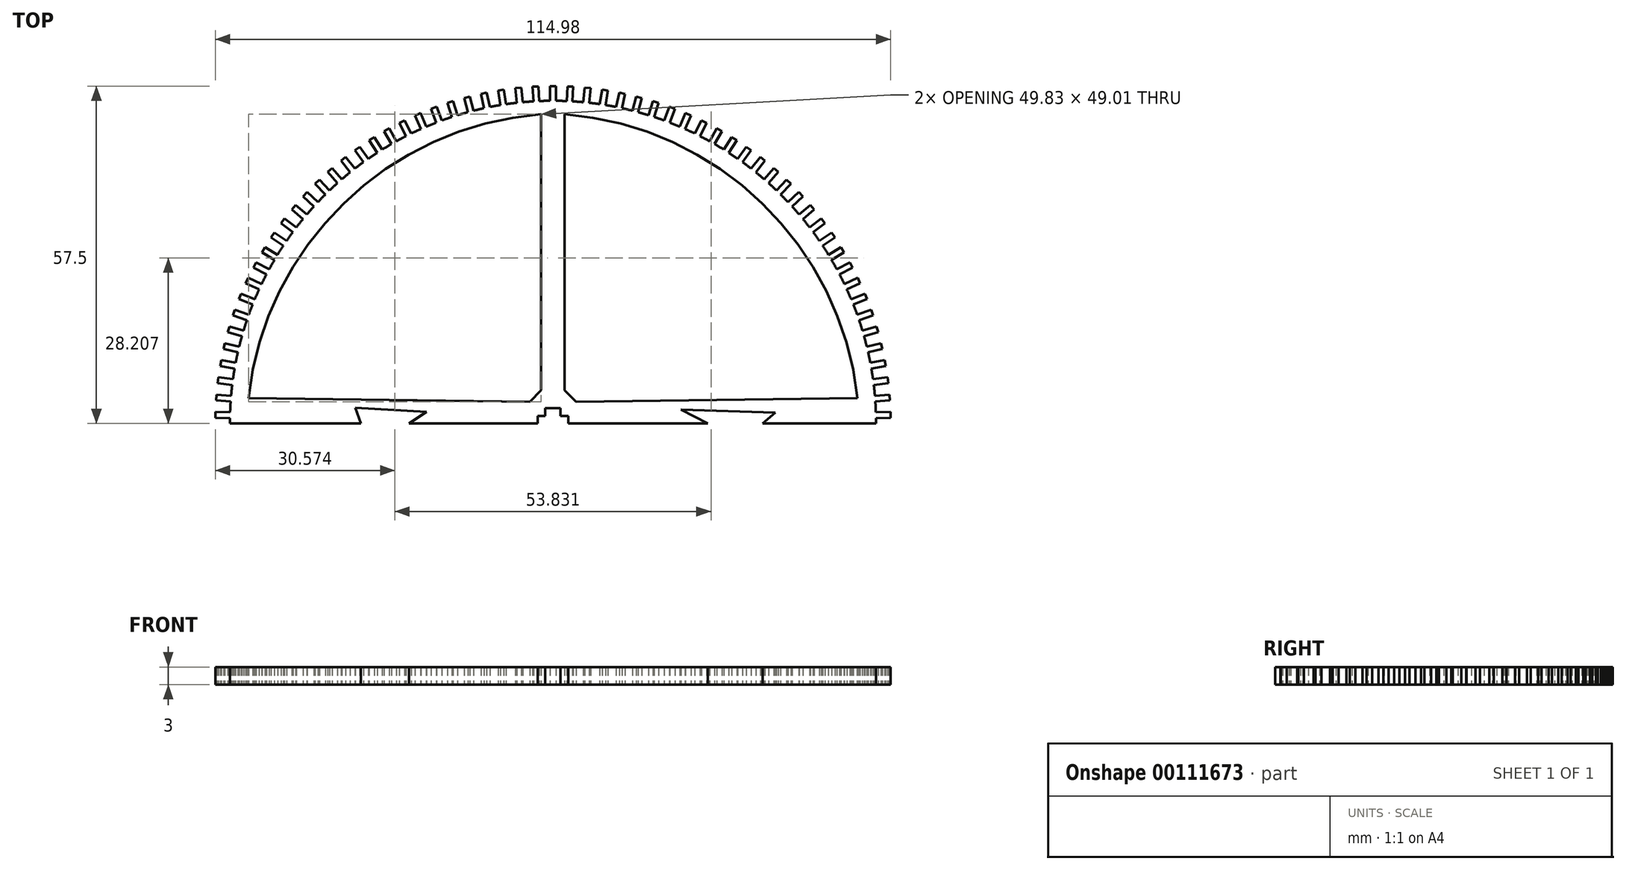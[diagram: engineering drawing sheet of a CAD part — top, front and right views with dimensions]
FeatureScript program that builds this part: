
annotation { "Feature Type Name" : "Feature", "Feature Type Description" : "" }
export const myFeature = defineFeature(function(context is Context, id is Id, definition is map)
    precondition{}
    {
        {
            var Q0;
            Q0=qCreatedBy(makeId("Top.planeOp"),FACE);
            var sketch = newSketch(context, id + "F0", { "sketchPlane" : qUnion([Q0])});
            skArc(sketch, "E0", {"start": v(55, 0.92) * mm, "mid": v(0, 55) * mm, "end": v(-55, 0.92) * mm});
            skLineSegment(sketch, "E1", {"start": v(0, 2.6) * mm, "end": v(1.3, 2.6) * mm});
            skLineSegment(sketch, "E2", {"start": v(1.3, 2.6) * mm, "end": v(1.3, 1.3) * mm});
            skLineSegment(sketch, "E3", {"start": v(1.3, 1.3) * mm, "end": v(2.6, 1.3) * mm});
            skLineSegment(sketch, "E4", {"start": v(2.6, 1.3) * mm, "end": v(2.6, 0) * mm});
            skLineSegment(sketch, "E5", {"start": v(-2.6, 1.3) * mm, "end": v(-1.3, 1.3) * mm});
            skLineSegment(sketch, "E6", {"start": v(-1.3, 1.3) * mm, "end": v(-1.3, 2.6) * mm});
            skLineSegment(sketch, "E7", {"start": v(-1.3, 2.6) * mm, "end": v(0, 2.6) * mm});
            skPoint(sketch, "E8.start.orphan", {"position": v(-51.96, 0) * mm});
            skPoint(sketch, "E9.endSnap0", {"position": v(-3.3, -4.33) * mm});
            skLineSegment(sketch, "E10.MirrorCS", {"start": v(-3.92, 3.7) * mm, "end": v(-51.83, 4.33) * mm});
            skArc(sketch, "E11.MirrorCS", {"start": v(-51.83, 4.33) * mm, "mid": v(-35.63, 37.5) * mm, "end": v(-2, 52.71) * mm});
            skLineSegment(sketch, "E12.MirrorCS", {"start": v(-2, 50.71) * mm, "end": v(-2, 5.66) * mm});
            skLineSegment(sketch, "E13.MirrorCS", {"start": v(-3.92, 3.7) * mm, "end": v(-2, 5.66) * mm});
            skLineSegment(sketch, "E14.MirrorCS", {"start": v(2, 50.71) * mm, "end": v(2, 5.66) * mm});
            skArc(sketch, "E15.MirrorCS", {"start": v(51.83, 4.33) * mm, "mid": v(35.63, 37.5) * mm, "end": v(2, 52.71) * mm});
            skLineSegment(sketch, "E16.MirrorCS", {"start": v(3.92, 3.7) * mm, "end": v(51.83, 4.33) * mm});
            skLineSegment(sketch, "E17.MirrorCS", {"start": v(3.92, 3.7) * mm, "end": v(2, 5.66) * mm});
            skLineSegment(sketch, "E18.MirrorCS", {"start": v(-2, 50.71) * mm, "end": v(-2, 52.71) * mm});
            skLineSegment(sketch, "E19.MirrorCS", {"start": v(2, 50.71) * mm, "end": v(2, 52.71) * mm});
            skLineSegment(sketch, "E20", {"start": v(0, 55) * mm, "end": v(0, 57.5) * mm});
            skLineSegment(sketch, "E21", {"start": v(0, 57.5) * mm, "end": v(0.5, 57.5) * mm});
            skLineSegment(sketch, "E22", {"start": v(0, 57.5) * mm, "end": v(-0.5, 57.5) * mm});
            skLineSegment(sketch, "E23", {"start": v(-0.5, 57.5) * mm, "end": v(-0.5, 55) * mm});
            skLineSegment(sketch, "E24", {"start": v(0.5, 57.5) * mm, "end": v(0.5, 55) * mm});
            skLineSegment(sketch, "E25.1.0", {"start": v(-2.46, 57.45) * mm, "end": v(-2.33, 54.95) * mm});
            skLineSegment(sketch, "E25.1.1", {"start": v(-3.46, 57.4) * mm, "end": v(-3.33, 54.9) * mm});
            skLineSegment(sketch, "E25.1.2", {"start": v(-2.96, 57.42) * mm, "end": v(-3.46, 57.4) * mm});
            skLineSegment(sketch, "E25.1.3", {"start": v(-2.96, 57.42) * mm, "end": v(-2.46, 57.45) * mm});
            skLineSegment(sketch, "E25.2.0", {"start": v(-5.41, 57.25) * mm, "end": v(-5.16, 54.76) * mm});
            skLineSegment(sketch, "E25.2.1", {"start": v(-6.4, 57.14) * mm, "end": v(-6.15, 54.65) * mm});
            skLineSegment(sketch, "E25.2.2", {"start": v(-5.91, 57.2) * mm, "end": v(-6.4, 57.14) * mm});
            skLineSegment(sketch, "E25.2.3", {"start": v(-5.91, 57.2) * mm, "end": v(-5.41, 57.25) * mm});
            skLineSegment(sketch, "E26.2.3.0", {"start": v(-8.35, 56.9) * mm, "end": v(-7.97, 54.42) * mm});
            skLineSegment(sketch, "E26.3.3.0", {"start": v(-9.34, 56.74) * mm, "end": v(-8.96, 54.27) * mm});
            skLineSegment(sketch, "E26.6.3.0", {"start": v(-8.85, 56.82) * mm, "end": v(-9.34, 56.74) * mm});
            skLineSegment(sketch, "E26.9.3.0", {"start": v(-8.85, 56.82) * mm, "end": v(-8.35, 56.9) * mm});
            skLineSegment(sketch, "E26.2.4.0", {"start": v(-11.27, 56.39) * mm, "end": v(-10.76, 53.94) * mm});
            skLineSegment(sketch, "E26.3.4.0", {"start": v(-12.25, 56.18) * mm, "end": v(-11.74, 53.73) * mm});
            skLineSegment(sketch, "E26.6.4.0", {"start": v(-11.76, 56.28) * mm, "end": v(-12.25, 56.18) * mm});
            skLineSegment(sketch, "E26.9.4.0", {"start": v(-11.76, 56.28) * mm, "end": v(-11.27, 56.39) * mm});
            skLineSegment(sketch, "E26.2.5.0", {"start": v(-14.16, 55.73) * mm, "end": v(-13.52, 53.31) * mm});
            skLineSegment(sketch, "E26.3.5.0", {"start": v(-15.13, 55.48) * mm, "end": v(-14.49, 53.06) * mm});
            skLineSegment(sketch, "E26.6.5.0", {"start": v(-14.64, 55.6) * mm, "end": v(-15.13, 55.48) * mm});
            skLineSegment(sketch, "E26.9.5.0", {"start": v(-14.64, 55.6) * mm, "end": v(-14.16, 55.73) * mm});
            skLineSegment(sketch, "E26.2.6.0", {"start": v(-17.01, 54.93) * mm, "end": v(-16.25, 52.54) * mm});
            skLineSegment(sketch, "E26.3.6.0", {"start": v(-17.96, 54.62) * mm, "end": v(-17.2, 52.24) * mm});
            skLineSegment(sketch, "E26.6.6.0", {"start": v(-17.49, 54.78) * mm, "end": v(-17.96, 54.62) * mm});
            skLineSegment(sketch, "E26.9.6.0", {"start": v(-17.49, 54.78) * mm, "end": v(-17.01, 54.93) * mm});
            skLineSegment(sketch, "E26.2.7.0", {"start": v(-19.82, 53.98) * mm, "end": v(-18.93, 51.64) * mm});
            skLineSegment(sketch, "E26.3.7.0", {"start": v(-20.75, 53.63) * mm, "end": v(-19.87, 51.29) * mm});
            skLineSegment(sketch, "E26.6.7.0", {"start": v(-20.28, 53.8) * mm, "end": v(-20.75, 53.63) * mm});
            skLineSegment(sketch, "E26.9.7.0", {"start": v(-20.28, 53.8) * mm, "end": v(-19.82, 53.98) * mm});
            skLineSegment(sketch, "E26.2.8.0", {"start": v(-22.57, 52.89) * mm, "end": v(-21.57, 50.6) * mm});
            skLineSegment(sketch, "E26.3.8.0", {"start": v(-23.48, 52.49) * mm, "end": v(-22.48, 50.2) * mm});
            skLineSegment(sketch, "E26.6.8.0", {"start": v(-23.03, 52.69) * mm, "end": v(-23.48, 52.49) * mm});
            skLineSegment(sketch, "E26.9.8.0", {"start": v(-23.03, 52.69) * mm, "end": v(-22.57, 52.89) * mm});
            skLineSegment(sketch, "E26.2.9.0", {"start": v(-25.26, 51.66) * mm, "end": v(-24.14, 49.42) * mm});
            skLineSegment(sketch, "E26.3.9.0", {"start": v(-26.16, 51.2) * mm, "end": v(-25.04, 48.97) * mm});
            skLineSegment(sketch, "E26.6.9.0", {"start": v(-25.7, 51.43) * mm, "end": v(-26.16, 51.2) * mm});
            skLineSegment(sketch, "E26.9.9.0", {"start": v(-25.7, 51.43) * mm, "end": v(-25.26, 51.66) * mm});
            skLineSegment(sketch, "E26.2.10.0", {"start": v(-27.89, 50.29) * mm, "end": v(-26.65, 48.1) * mm});
            skLineSegment(sketch, "E26.3.10.0", {"start": v(-28.76, 49.8) * mm, "end": v(-27.52, 47.62) * mm});
            skLineSegment(sketch, "E26.6.10.0", {"start": v(-28.32, 50.04) * mm, "end": v(-28.76, 49.8) * mm});
            skLineSegment(sketch, "E26.9.10.0", {"start": v(-28.32, 50.04) * mm, "end": v(-27.89, 50.29) * mm});
            skLineSegment(sketch, "E26.2.11.0", {"start": v(-30.44, 48.79) * mm, "end": v(-29.1, 46.67) * mm});
            skLineSegment(sketch, "E26.3.11.0", {"start": v(-31.28, 48.25) * mm, "end": v(-29.94, 46.14) * mm});
            skLineSegment(sketch, "E26.6.11.0", {"start": v(-30.86, 48.52) * mm, "end": v(-31.28, 48.25) * mm});
            skLineSegment(sketch, "E26.9.11.0", {"start": v(-30.86, 48.52) * mm, "end": v(-30.44, 48.79) * mm});
            skLineSegment(sketch, "E26.2.12.0", {"start": v(-32.9, 47.15) * mm, "end": v(-31.46, 45.11) * mm});
            skLineSegment(sketch, "E26.3.12.0", {"start": v(-33.72, 46.57) * mm, "end": v(-32.27, 44.53) * mm});
            skLineSegment(sketch, "E26.6.12.0", {"start": v(-33.32, 46.86) * mm, "end": v(-33.72, 46.57) * mm});
            skLineSegment(sketch, "E26.9.12.0", {"start": v(-33.32, 46.86) * mm, "end": v(-32.9, 47.15) * mm});
            skLineSegment(sketch, "E26.2.13.0", {"start": v(-35.3, 45.4) * mm, "end": v(-33.74, 43.44) * mm});
            skLineSegment(sketch, "E26.3.13.0", {"start": v(-36.08, 44.78) * mm, "end": v(-34.52, 42.81) * mm});
            skLineSegment(sketch, "E26.6.13.0", {"start": v(-35.69, 45.09) * mm, "end": v(-36.08, 44.78) * mm});
            skLineSegment(sketch, "E26.9.13.0", {"start": v(-35.69, 45.09) * mm, "end": v(-35.3, 45.4) * mm});
            skLineSegment(sketch, "E26.2.14.0", {"start": v(-37.58, 43.52) * mm, "end": v(-35.93, 41.64) * mm});
            skLineSegment(sketch, "E26.3.14.0", {"start": v(-38.33, 42.86) * mm, "end": v(-36.68, 40.98) * mm});
            skLineSegment(sketch, "E26.6.14.0", {"start": v(-37.96, 43.2) * mm, "end": v(-38.33, 42.86) * mm});
            skLineSegment(sketch, "E26.9.14.0", {"start": v(-37.96, 43.2) * mm, "end": v(-37.58, 43.52) * mm});
            skLineSegment(sketch, "E26.2.15.0", {"start": v(-39.77, 41.53) * mm, "end": v(-38.03, 39.74) * mm});
            skLineSegment(sketch, "E26.3.15.0", {"start": v(-40.49, 40.83) * mm, "end": v(-38.74, 39.04) * mm});
            skLineSegment(sketch, "E26.6.15.0", {"start": v(-40.13, 41.18) * mm, "end": v(-40.49, 40.83) * mm});
            skLineSegment(sketch, "E26.9.15.0", {"start": v(-40.13, 41.18) * mm, "end": v(-39.77, 41.53) * mm});
            skLineSegment(sketch, "E26.2.16.0", {"start": v(-41.86, 39.43) * mm, "end": v(-40.02, 37.73) * mm});
            skLineSegment(sketch, "E26.3.16.0", {"start": v(-42.54, 38.7) * mm, "end": v(-40.7, 37) * mm});
            skLineSegment(sketch, "E26.6.16.0", {"start": v(-42.2, 39.06) * mm, "end": v(-42.54, 38.7) * mm});
            skLineSegment(sketch, "E26.9.16.0", {"start": v(-42.2, 39.06) * mm, "end": v(-41.86, 39.43) * mm});
            skLineSegment(sketch, "E26.2.17.0", {"start": v(-43.83, 37.22) * mm, "end": v(-41.91, 35.62) * mm});
            skLineSegment(sketch, "E26.3.17.0", {"start": v(-44.47, 36.45) * mm, "end": v(-42.55, 34.85) * mm});
            skLineSegment(sketch, "E26.6.17.0", {"start": v(-44.15, 36.83) * mm, "end": v(-44.47, 36.45) * mm});
            skLineSegment(sketch, "E26.9.17.0", {"start": v(-44.15, 36.83) * mm, "end": v(-43.83, 37.22) * mm});
            skLineSegment(sketch, "E26.2.18.0", {"start": v(-45.7, 34.91) * mm, "end": v(-43.69, 33.41) * mm});
            skLineSegment(sketch, "E26.3.18.0", {"start": v(-46.3, 34.11) * mm, "end": v(-44.29, 32.61) * mm});
            skLineSegment(sketch, "E26.6.18.0", {"start": v(-46, 34.51) * mm, "end": v(-46.3, 34.11) * mm});
            skLineSegment(sketch, "E26.9.18.0", {"start": v(-46, 34.51) * mm, "end": v(-45.7, 34.91) * mm});
            skLineSegment(sketch, "E26.2.19.0", {"start": v(-47.43, 32.51) * mm, "end": v(-45.35, 31.12) * mm});
            skLineSegment(sketch, "E26.3.19.0", {"start": v(-47.99, 31.68) * mm, "end": v(-45.9, 30.29) * mm});
            skLineSegment(sketch, "E26.6.19.0", {"start": v(-47.7, 32.1) * mm, "end": v(-47.99, 31.68) * mm});
            skLineSegment(sketch, "E26.9.19.0", {"start": v(-47.7, 32.1) * mm, "end": v(-47.43, 32.51) * mm});
            skLineSegment(sketch, "E26.2.20.0", {"start": v(-49.04, 30.03) * mm, "end": v(-46.9, 28.74) * mm});
            skLineSegment(sketch, "E26.3.20.0", {"start": v(-49.55, 29.17) * mm, "end": v(-47.4, 27.88) * mm});
            skLineSegment(sketch, "E26.6.20.0", {"start": v(-49.3, 29.6) * mm, "end": v(-49.55, 29.17) * mm});
            skLineSegment(sketch, "E26.9.20.0", {"start": v(-49.3, 29.6) * mm, "end": v(-49.04, 30.03) * mm});
            skLineSegment(sketch, "E26.2.21.0", {"start": v(-50.52, 27.47) * mm, "end": v(-48.31, 26.29) * mm});
            skLineSegment(sketch, "E26.3.21.0", {"start": v(-50.99, 26.58) * mm, "end": v(-48.78, 25.4) * mm});
            skLineSegment(sketch, "E26.6.21.0", {"start": v(-50.75, 27.02) * mm, "end": v(-50.99, 26.58) * mm});
            skLineSegment(sketch, "E26.9.21.0", {"start": v(-50.75, 27.02) * mm, "end": v(-50.52, 27.47) * mm});
            skLineSegment(sketch, "E26.2.22.0", {"start": v(-51.87, 24.83) * mm, "end": v(-49.6, 23.77) * mm});
            skLineSegment(sketch, "E26.3.22.0", {"start": v(-52.29, 23.92) * mm, "end": v(-50.02, 22.86) * mm});
            skLineSegment(sketch, "E26.6.22.0", {"start": v(-52.08, 24.38) * mm, "end": v(-52.29, 23.92) * mm});
            skLineSegment(sketch, "E26.9.22.0", {"start": v(-52.08, 24.38) * mm, "end": v(-51.87, 24.83) * mm});
            skLineSegment(sketch, "E26.2.23.0", {"start": v(-53.08, 22.13) * mm, "end": v(-50.76, 21.18) * mm});
            skLineSegment(sketch, "E26.3.23.0", {"start": v(-53.45, 21.2) * mm, "end": v(-51.13, 20.26) * mm});
            skLineSegment(sketch, "E26.6.23.0", {"start": v(-53.26, 21.66) * mm, "end": v(-53.45, 21.2) * mm});
            skLineSegment(sketch, "E26.9.23.0", {"start": v(-53.26, 21.66) * mm, "end": v(-53.08, 22.13) * mm});
            skLineSegment(sketch, "E26.2.24.0", {"start": v(-54.14, 19.36) * mm, "end": v(-51.78, 18.54) * mm});
            skLineSegment(sketch, "E26.3.24.0", {"start": v(-54.47, 18.42) * mm, "end": v(-52.1, 17.6) * mm});
            skLineSegment(sketch, "E26.6.24.0", {"start": v(-54.3, 18.9) * mm, "end": v(-54.47, 18.42) * mm});
            skLineSegment(sketch, "E26.9.24.0", {"start": v(-54.3, 18.9) * mm, "end": v(-54.14, 19.36) * mm});
            skLineSegment(sketch, "E26.2.25.0", {"start": v(-55.07, 16.55) * mm, "end": v(-52.67, 15.85) * mm});
            skLineSegment(sketch, "E26.3.25.0", {"start": v(-55.35, 15.6) * mm, "end": v(-52.95, 14.9) * mm});
            skLineSegment(sketch, "E26.6.25.0", {"start": v(-55.2, 16.07) * mm, "end": v(-55.35, 15.6) * mm});
            skLineSegment(sketch, "E26.9.25.0", {"start": v(-55.2, 16.07) * mm, "end": v(-55.07, 16.55) * mm});
            skLineSegment(sketch, "E26.2.26.0", {"start": v(-55.85, 13.7) * mm, "end": v(-53.41, 13.12) * mm});
            skLineSegment(sketch, "E26.3.26.0", {"start": v(-56.08, 12.72) * mm, "end": v(-53.64, 12.15) * mm});
            skLineSegment(sketch, "E26.6.26.0", {"start": v(-55.96, 13.2) * mm, "end": v(-56.08, 12.72) * mm});
            skLineSegment(sketch, "E26.9.26.0", {"start": v(-55.96, 13.2) * mm, "end": v(-55.85, 13.7) * mm});
            skLineSegment(sketch, "E26.2.27.0", {"start": v(-56.48, 10.8) * mm, "end": v(-54.02, 10.35) * mm});
            skLineSegment(sketch, "E26.3.27.0", {"start": v(-56.66, 9.82) * mm, "end": v(-54.2, 9.37) * mm});
            skLineSegment(sketch, "E26.6.27.0", {"start": v(-56.57, 10.3) * mm, "end": v(-56.66, 9.82) * mm});
            skLineSegment(sketch, "E26.9.27.0", {"start": v(-56.57, 10.3) * mm, "end": v(-56.48, 10.8) * mm});
            skLineSegment(sketch, "E26.2.28.0", {"start": v(-56.96, 7.88) * mm, "end": v(-54.48, 7.56) * mm});
            skLineSegment(sketch, "E26.3.28.0", {"start": v(-57.09, 6.89) * mm, "end": v(-54.6, 6.57) * mm});
            skLineSegment(sketch, "E26.6.28.0", {"start": v(-57.02, 7.38) * mm, "end": v(-57.09, 6.89) * mm});
            skLineSegment(sketch, "E26.9.28.0", {"start": v(-57.02, 7.38) * mm, "end": v(-56.96, 7.88) * mm});
            skLineSegment(sketch, "E26.2.29.0", {"start": v(-57.29, 4.94) * mm, "end": v(-54.8, 4.74) * mm});
            skLineSegment(sketch, "E26.3.29.0", {"start": v(-57.37, 3.94) * mm, "end": v(-54.87, 3.75) * mm});
            skLineSegment(sketch, "E26.6.29.0", {"start": v(-57.33, 4.44) * mm, "end": v(-57.37, 3.94) * mm});
            skLineSegment(sketch, "E26.9.29.0", {"start": v(-57.33, 4.44) * mm, "end": v(-57.29, 4.94) * mm});
            skLineSegment(sketch, "E26.2.30.0", {"start": v(-57.47, 1.98) * mm, "end": v(-54.97, 1.92) * mm});
            skLineSegment(sketch, "E26.3.30.0", {"start": v(-57.5, 0.98) * mm, "end": v(-55, 0.92) * mm});
            skLineSegment(sketch, "E26.6.30.0", {"start": v(-57.48, 1.48) * mm, "end": v(-57.5, 0.98) * mm});
            skLineSegment(sketch, "E26.9.30.0", {"start": v(-57.48, 1.48) * mm, "end": v(-57.47, 1.98) * mm});
            skLineSegment(sketch, "E26.2.92.0", {"start": v(57.5, 0.98) * mm, "end": v(55, 0.92) * mm});
            skLineSegment(sketch, "E26.3.92.0", {"start": v(57.47, 1.98) * mm, "end": v(54.97, 1.92) * mm});
            skLineSegment(sketch, "E26.6.92.0", {"start": v(57.48, 1.48) * mm, "end": v(57.47, 1.98) * mm});
            skLineSegment(sketch, "E26.9.92.0", {"start": v(57.48, 1.48) * mm, "end": v(57.5, 0.98) * mm});
            skLineSegment(sketch, "E26.2.93.0", {"start": v(57.37, 3.94) * mm, "end": v(54.87, 3.75) * mm});
            skLineSegment(sketch, "E26.3.93.0", {"start": v(57.29, 4.94) * mm, "end": v(54.8, 4.74) * mm});
            skLineSegment(sketch, "E26.6.93.0", {"start": v(57.33, 4.44) * mm, "end": v(57.29, 4.94) * mm});
            skLineSegment(sketch, "E26.9.93.0", {"start": v(57.33, 4.44) * mm, "end": v(57.37, 3.94) * mm});
            skLineSegment(sketch, "E26.2.94.0", {"start": v(57.09, 6.89) * mm, "end": v(54.6, 6.57) * mm});
            skLineSegment(sketch, "E26.3.94.0", {"start": v(56.96, 7.88) * mm, "end": v(54.48, 7.56) * mm});
            skLineSegment(sketch, "E26.6.94.0", {"start": v(57.02, 7.38) * mm, "end": v(56.96, 7.88) * mm});
            skLineSegment(sketch, "E26.9.94.0", {"start": v(57.02, 7.38) * mm, "end": v(57.09, 6.89) * mm});
            skLineSegment(sketch, "E26.2.95.0", {"start": v(56.66, 9.82) * mm, "end": v(54.2, 9.37) * mm});
            skLineSegment(sketch, "E26.3.95.0", {"start": v(56.48, 10.8) * mm, "end": v(54.02, 10.35) * mm});
            skLineSegment(sketch, "E26.6.95.0", {"start": v(56.57, 10.3) * mm, "end": v(56.48, 10.8) * mm});
            skLineSegment(sketch, "E26.9.95.0", {"start": v(56.57, 10.3) * mm, "end": v(56.66, 9.82) * mm});
            skLineSegment(sketch, "E26.2.96.0", {"start": v(56.08, 12.72) * mm, "end": v(53.64, 12.15) * mm});
            skLineSegment(sketch, "E26.3.96.0", {"start": v(55.85, 13.7) * mm, "end": v(53.41, 13.12) * mm});
            skLineSegment(sketch, "E26.6.96.0", {"start": v(55.96, 13.2) * mm, "end": v(55.85, 13.7) * mm});
            skLineSegment(sketch, "E26.9.96.0", {"start": v(55.96, 13.2) * mm, "end": v(56.08, 12.72) * mm});
            skLineSegment(sketch, "E26.2.97.0", {"start": v(55.35, 15.6) * mm, "end": v(52.95, 14.9) * mm});
            skLineSegment(sketch, "E26.3.97.0", {"start": v(55.07, 16.55) * mm, "end": v(52.67, 15.85) * mm});
            skLineSegment(sketch, "E26.6.97.0", {"start": v(55.2, 16.07) * mm, "end": v(55.07, 16.55) * mm});
            skLineSegment(sketch, "E26.9.97.0", {"start": v(55.2, 16.07) * mm, "end": v(55.35, 15.6) * mm});
            skLineSegment(sketch, "E26.2.98.0", {"start": v(54.47, 18.42) * mm, "end": v(52.1, 17.6) * mm});
            skLineSegment(sketch, "E26.3.98.0", {"start": v(54.14, 19.36) * mm, "end": v(51.78, 18.54) * mm});
            skLineSegment(sketch, "E26.6.98.0", {"start": v(54.3, 18.9) * mm, "end": v(54.14, 19.36) * mm});
            skLineSegment(sketch, "E26.9.98.0", {"start": v(54.3, 18.9) * mm, "end": v(54.47, 18.42) * mm});
            skLineSegment(sketch, "E26.2.99.0", {"start": v(53.45, 21.2) * mm, "end": v(51.13, 20.26) * mm});
            skLineSegment(sketch, "E26.3.99.0", {"start": v(53.08, 22.13) * mm, "end": v(50.76, 21.18) * mm});
            skLineSegment(sketch, "E26.6.99.0", {"start": v(53.26, 21.66) * mm, "end": v(53.08, 22.13) * mm});
            skLineSegment(sketch, "E26.9.99.0", {"start": v(53.26, 21.66) * mm, "end": v(53.45, 21.2) * mm});
            skLineSegment(sketch, "E26.2.100.0", {"start": v(52.29, 23.92) * mm, "end": v(50.02, 22.86) * mm});
            skLineSegment(sketch, "E26.3.100.0", {"start": v(51.87, 24.83) * mm, "end": v(49.6, 23.77) * mm});
            skLineSegment(sketch, "E26.6.100.0", {"start": v(52.08, 24.38) * mm, "end": v(51.87, 24.83) * mm});
            skLineSegment(sketch, "E26.9.100.0", {"start": v(52.08, 24.38) * mm, "end": v(52.29, 23.92) * mm});
            skLineSegment(sketch, "E26.2.101.0", {"start": v(50.99, 26.58) * mm, "end": v(48.78, 25.4) * mm});
            skLineSegment(sketch, "E26.3.101.0", {"start": v(50.52, 27.47) * mm, "end": v(48.31, 26.29) * mm});
            skLineSegment(sketch, "E26.6.101.0", {"start": v(50.75, 27.02) * mm, "end": v(50.52, 27.47) * mm});
            skLineSegment(sketch, "E26.9.101.0", {"start": v(50.75, 27.02) * mm, "end": v(50.99, 26.58) * mm});
            skLineSegment(sketch, "E26.2.102.0", {"start": v(49.55, 29.17) * mm, "end": v(47.4, 27.88) * mm});
            skLineSegment(sketch, "E26.3.102.0", {"start": v(49.04, 30.03) * mm, "end": v(46.9, 28.74) * mm});
            skLineSegment(sketch, "E26.6.102.0", {"start": v(49.3, 29.6) * mm, "end": v(49.04, 30.03) * mm});
            skLineSegment(sketch, "E26.9.102.0", {"start": v(49.3, 29.6) * mm, "end": v(49.55, 29.17) * mm});
            skLineSegment(sketch, "E26.2.103.0", {"start": v(47.99, 31.68) * mm, "end": v(45.9, 30.29) * mm});
            skLineSegment(sketch, "E26.3.103.0", {"start": v(47.43, 32.51) * mm, "end": v(45.35, 31.12) * mm});
            skLineSegment(sketch, "E26.6.103.0", {"start": v(47.7, 32.1) * mm, "end": v(47.43, 32.51) * mm});
            skLineSegment(sketch, "E26.9.103.0", {"start": v(47.7, 32.1) * mm, "end": v(47.99, 31.68) * mm});
            skLineSegment(sketch, "E26.2.104.0", {"start": v(46.3, 34.11) * mm, "end": v(44.29, 32.61) * mm});
            skLineSegment(sketch, "E26.3.104.0", {"start": v(45.7, 34.91) * mm, "end": v(43.69, 33.41) * mm});
            skLineSegment(sketch, "E26.6.104.0", {"start": v(46, 34.51) * mm, "end": v(45.7, 34.91) * mm});
            skLineSegment(sketch, "E26.9.104.0", {"start": v(46, 34.51) * mm, "end": v(46.3, 34.11) * mm});
            skLineSegment(sketch, "E26.2.105.0", {"start": v(44.47, 36.45) * mm, "end": v(42.55, 34.85) * mm});
            skLineSegment(sketch, "E26.3.105.0", {"start": v(43.83, 37.22) * mm, "end": v(41.91, 35.62) * mm});
            skLineSegment(sketch, "E26.6.105.0", {"start": v(44.15, 36.83) * mm, "end": v(43.83, 37.22) * mm});
            skLineSegment(sketch, "E26.9.105.0", {"start": v(44.15, 36.83) * mm, "end": v(44.47, 36.45) * mm});
            skLineSegment(sketch, "E26.2.106.0", {"start": v(42.54, 38.7) * mm, "end": v(40.7, 37) * mm});
            skLineSegment(sketch, "E26.3.106.0", {"start": v(41.86, 39.43) * mm, "end": v(40.02, 37.73) * mm});
            skLineSegment(sketch, "E26.6.106.0", {"start": v(42.2, 39.06) * mm, "end": v(41.86, 39.43) * mm});
            skLineSegment(sketch, "E26.9.106.0", {"start": v(42.2, 39.06) * mm, "end": v(42.54, 38.7) * mm});
            skLineSegment(sketch, "E26.2.107.0", {"start": v(40.49, 40.83) * mm, "end": v(38.74, 39.04) * mm});
            skLineSegment(sketch, "E26.3.107.0", {"start": v(39.77, 41.53) * mm, "end": v(38.03, 39.74) * mm});
            skLineSegment(sketch, "E26.6.107.0", {"start": v(40.13, 41.18) * mm, "end": v(39.77, 41.53) * mm});
            skLineSegment(sketch, "E26.9.107.0", {"start": v(40.13, 41.18) * mm, "end": v(40.49, 40.83) * mm});
            skLineSegment(sketch, "E26.2.108.0", {"start": v(38.33, 42.86) * mm, "end": v(36.68, 40.98) * mm});
            skLineSegment(sketch, "E26.3.108.0", {"start": v(37.58, 43.52) * mm, "end": v(35.93, 41.64) * mm});
            skLineSegment(sketch, "E26.6.108.0", {"start": v(37.96, 43.2) * mm, "end": v(37.58, 43.52) * mm});
            skLineSegment(sketch, "E26.9.108.0", {"start": v(37.96, 43.2) * mm, "end": v(38.33, 42.86) * mm});
            skLineSegment(sketch, "E26.2.109.0", {"start": v(36.08, 44.78) * mm, "end": v(34.52, 42.81) * mm});
            skLineSegment(sketch, "E26.3.109.0", {"start": v(35.3, 45.4) * mm, "end": v(33.74, 43.44) * mm});
            skLineSegment(sketch, "E26.6.109.0", {"start": v(35.69, 45.09) * mm, "end": v(35.3, 45.4) * mm});
            skLineSegment(sketch, "E26.9.109.0", {"start": v(35.69, 45.09) * mm, "end": v(36.08, 44.78) * mm});
            skLineSegment(sketch, "E26.2.110.0", {"start": v(33.72, 46.57) * mm, "end": v(32.27, 44.53) * mm});
            skLineSegment(sketch, "E26.3.110.0", {"start": v(32.9, 47.15) * mm, "end": v(31.46, 45.11) * mm});
            skLineSegment(sketch, "E26.6.110.0", {"start": v(33.32, 46.86) * mm, "end": v(32.9, 47.15) * mm});
            skLineSegment(sketch, "E26.9.110.0", {"start": v(33.32, 46.86) * mm, "end": v(33.72, 46.57) * mm});
            skLineSegment(sketch, "E26.2.111.0", {"start": v(31.28, 48.25) * mm, "end": v(29.94, 46.14) * mm});
            skLineSegment(sketch, "E26.3.111.0", {"start": v(30.44, 48.79) * mm, "end": v(29.1, 46.67) * mm});
            skLineSegment(sketch, "E26.6.111.0", {"start": v(30.86, 48.52) * mm, "end": v(30.44, 48.79) * mm});
            skLineSegment(sketch, "E26.9.111.0", {"start": v(30.86, 48.52) * mm, "end": v(31.28, 48.25) * mm});
            skLineSegment(sketch, "E26.2.112.0", {"start": v(28.76, 49.8) * mm, "end": v(27.52, 47.62) * mm});
            skLineSegment(sketch, "E26.3.112.0", {"start": v(27.89, 50.29) * mm, "end": v(26.65, 48.1) * mm});
            skLineSegment(sketch, "E26.6.112.0", {"start": v(28.32, 50.04) * mm, "end": v(27.89, 50.29) * mm});
            skLineSegment(sketch, "E26.9.112.0", {"start": v(28.32, 50.04) * mm, "end": v(28.76, 49.8) * mm});
            skLineSegment(sketch, "E26.2.113.0", {"start": v(26.16, 51.2) * mm, "end": v(25.04, 48.97) * mm});
            skLineSegment(sketch, "E26.3.113.0", {"start": v(25.26, 51.66) * mm, "end": v(24.14, 49.42) * mm});
            skLineSegment(sketch, "E26.6.113.0", {"start": v(25.7, 51.43) * mm, "end": v(25.26, 51.66) * mm});
            skLineSegment(sketch, "E26.9.113.0", {"start": v(25.7, 51.43) * mm, "end": v(26.16, 51.2) * mm});
            skLineSegment(sketch, "E26.2.114.0", {"start": v(23.48, 52.49) * mm, "end": v(22.48, 50.2) * mm});
            skLineSegment(sketch, "E26.3.114.0", {"start": v(22.57, 52.89) * mm, "end": v(21.57, 50.6) * mm});
            skLineSegment(sketch, "E26.6.114.0", {"start": v(23.03, 52.69) * mm, "end": v(22.57, 52.89) * mm});
            skLineSegment(sketch, "E26.9.114.0", {"start": v(23.03, 52.69) * mm, "end": v(23.48, 52.49) * mm});
            skLineSegment(sketch, "E26.2.115.0", {"start": v(20.75, 53.63) * mm, "end": v(19.87, 51.29) * mm});
            skLineSegment(sketch, "E26.3.115.0", {"start": v(19.82, 53.98) * mm, "end": v(18.93, 51.64) * mm});
            skLineSegment(sketch, "E26.6.115.0", {"start": v(20.28, 53.8) * mm, "end": v(19.82, 53.98) * mm});
            skLineSegment(sketch, "E26.9.115.0", {"start": v(20.28, 53.8) * mm, "end": v(20.75, 53.63) * mm});
            skLineSegment(sketch, "E26.2.116.0", {"start": v(17.96, 54.62) * mm, "end": v(17.2, 52.24) * mm});
            skLineSegment(sketch, "E26.3.116.0", {"start": v(17.01, 54.93) * mm, "end": v(16.25, 52.54) * mm});
            skLineSegment(sketch, "E26.6.116.0", {"start": v(17.49, 54.78) * mm, "end": v(17.01, 54.93) * mm});
            skLineSegment(sketch, "E26.9.116.0", {"start": v(17.49, 54.78) * mm, "end": v(17.96, 54.62) * mm});
            skLineSegment(sketch, "E26.2.117.0", {"start": v(15.13, 55.48) * mm, "end": v(14.49, 53.06) * mm});
            skLineSegment(sketch, "E26.3.117.0", {"start": v(14.16, 55.73) * mm, "end": v(13.52, 53.31) * mm});
            skLineSegment(sketch, "E26.6.117.0", {"start": v(14.64, 55.6) * mm, "end": v(14.16, 55.73) * mm});
            skLineSegment(sketch, "E26.9.117.0", {"start": v(14.64, 55.6) * mm, "end": v(15.13, 55.48) * mm});
            skLineSegment(sketch, "E26.2.118.0", {"start": v(12.25, 56.18) * mm, "end": v(11.74, 53.73) * mm});
            skLineSegment(sketch, "E26.3.118.0", {"start": v(11.27, 56.39) * mm, "end": v(10.76, 53.94) * mm});
            skLineSegment(sketch, "E26.6.118.0", {"start": v(11.76, 56.28) * mm, "end": v(11.27, 56.39) * mm});
            skLineSegment(sketch, "E26.9.118.0", {"start": v(11.76, 56.28) * mm, "end": v(12.25, 56.18) * mm});
            skLineSegment(sketch, "E26.2.119.0", {"start": v(9.34, 56.74) * mm, "end": v(8.96, 54.27) * mm});
            skLineSegment(sketch, "E26.3.119.0", {"start": v(8.35, 56.9) * mm, "end": v(7.97, 54.42) * mm});
            skLineSegment(sketch, "E26.6.119.0", {"start": v(8.85, 56.82) * mm, "end": v(8.35, 56.9) * mm});
            skLineSegment(sketch, "E26.9.119.0", {"start": v(8.85, 56.82) * mm, "end": v(9.34, 56.74) * mm});
            skLineSegment(sketch, "E27.2.120.0", {"start": v(6.4, 57.14) * mm, "end": v(6.15, 54.65) * mm});
            skLineSegment(sketch, "E27.3.120.0", {"start": v(5.41, 57.25) * mm, "end": v(5.16, 54.76) * mm});
            skLineSegment(sketch, "E27.6.120.0", {"start": v(5.91, 57.2) * mm, "end": v(5.41, 57.25) * mm});
            skLineSegment(sketch, "E27.9.120.0", {"start": v(5.91, 57.2) * mm, "end": v(6.4, 57.14) * mm});
            skLineSegment(sketch, "E27.2.121.0", {"start": v(3.46, 57.4) * mm, "end": v(3.33, 54.9) * mm});
            skLineSegment(sketch, "E27.3.121.0", {"start": v(2.46, 57.45) * mm, "end": v(2.33, 54.95) * mm});
            skLineSegment(sketch, "E27.6.121.0", {"start": v(2.96, 57.42) * mm, "end": v(2.46, 57.45) * mm});
            skLineSegment(sketch, "E27.9.121.0", {"start": v(2.96, 57.42) * mm, "end": v(3.46, 57.4) * mm});
            skLineSegment(sketch, "E28", {"start": v(-55, 0) * mm, "end": v(-32.7, 0) * mm});
            skLineSegment(sketch, "E29", {"start": v(35.68, 0) * mm, "end": v(37.88, 1.86) * mm});
            skLineSegment(sketch, "E30", {"start": v(37.88, 1.86) * mm, "end": v(21.75, 2.38) * mm});
            skLineSegment(sketch, "E31", {"start": v(21.75, 2.38) * mm, "end": v(26.37, 0) * mm});
            skLineSegment(sketch, "E32", {"start": v(-24.52, 0) * mm, "end": v(-21.56, 2.01) * mm});
            skLineSegment(sketch, "E33", {"start": v(-21.56, 2.01) * mm, "end": v(-33.67, 2.7) * mm});
            skLineSegment(sketch, "E34", {"start": v(-33.67, 2.7) * mm, "end": v(-32.7, 0) * mm});
            skLineSegment(sketch, "E35.trimOffspring", {"start": v(35.68, 0) * mm, "end": v(55, 0) * mm});
            skLineSegment(sketch, "E36", {"start": v(-55, 0) * mm, "end": v(-51.96, 0) * mm});
            skLineSegment(sketch, "E37", {"start": v(55, 0) * mm, "end": v(50.18, 0) * mm});
            skLineSegment(sketch, "E38", {"start": v(55, 0.92) * mm, "end": v(55, 0) * mm});
            skLineSegment(sketch, "E39", {"start": v(-55, 0.92) * mm, "end": v(-55, 0) * mm});
            skLineSegment(sketch, "E40", {"start": v(-2.6, 1.3) * mm, "end": v(-2.6, 0) * mm});
            skLineSegment(sketch, "E41.trimOffspring", {"start": v(2.6, 0) * mm, "end": v(26.37, 0) * mm});
            skLineSegment(sketch, "E42", {"start": v(-2.6, 0) * mm, "end": v(-24.52, 0) * mm});
            skSolve(sketch);
        }
        {
            var Q0;
            Q0 = qSketchRegion(id + "F0", true);
            extrude(context, id + "F1", {"entities" : qUnion([Q0]), "depth" : 3 * mm});
        }
    });
